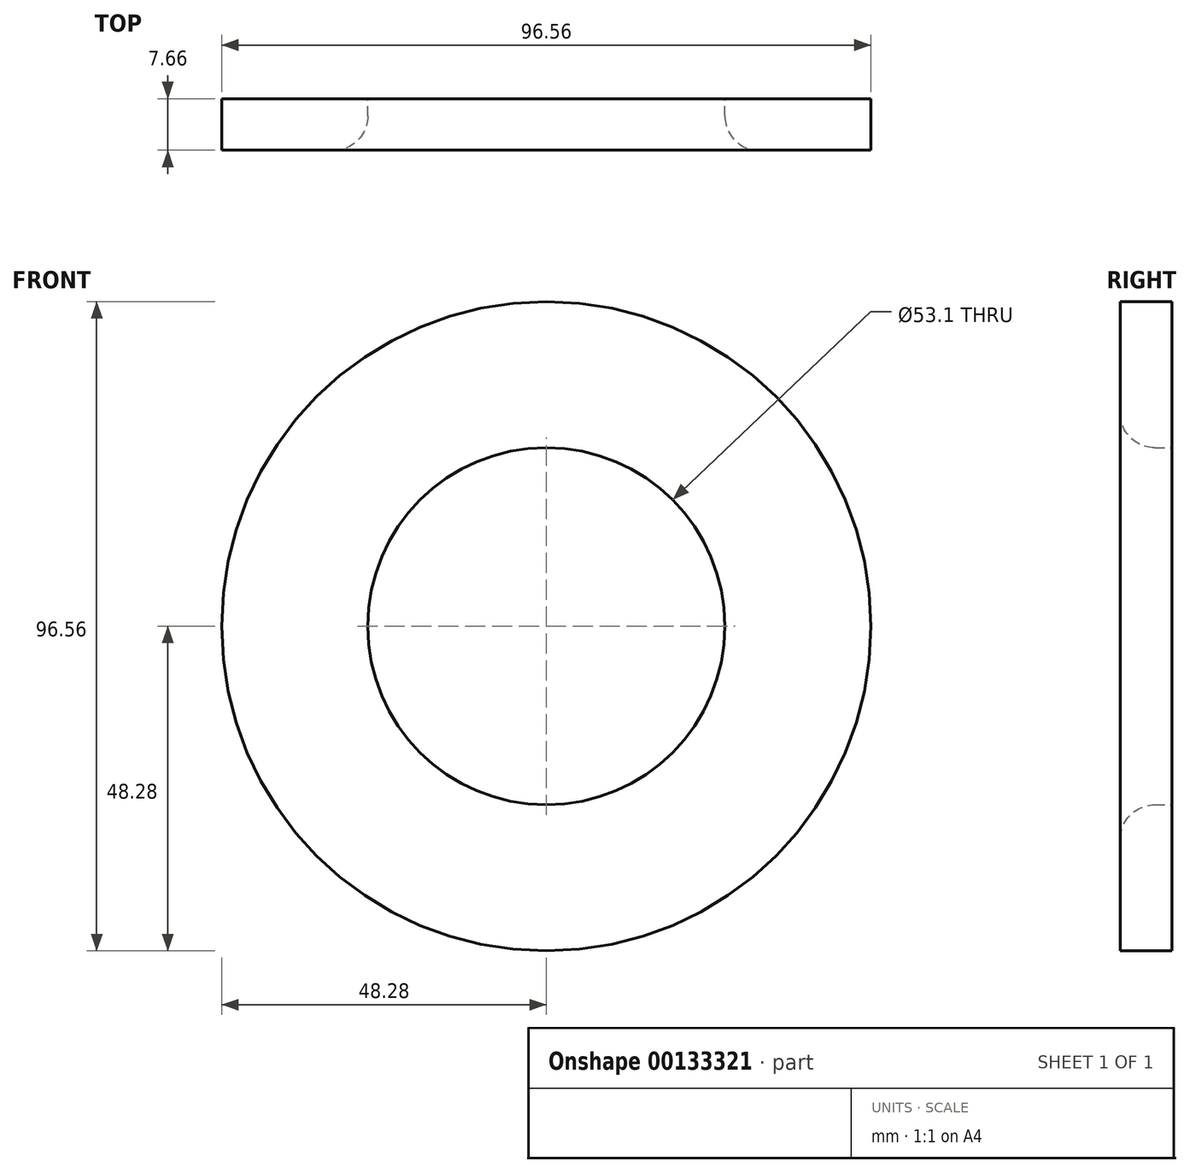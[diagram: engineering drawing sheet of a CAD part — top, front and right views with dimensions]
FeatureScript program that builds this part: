
annotation { "Feature Type Name" : "Feature", "Feature Type Description" : "" }
export const myFeature = defineFeature(function(context is Context, id is Id, definition is map)
    precondition{}
    {
        {
            var Q0;
            Q0=qCreatedBy(makeId("Front.planeOp"),FACE);
            var sketch = newSketch(context, id + "F0", { "sketchPlane" : qUnion([Q0])});
            skCircle(sketch, "E0", {"center": v(0, 0) * mm, "radius": 48.28 * mm});
            skCircle(sketch, "E1.0", {"center": v(0, 0) * mm, "radius": 26.55 * mm});
            skCircle(sketch, "E2.0", {"center": v(0, 0) * mm, "radius": 15.59 * mm});
            skCircle(sketch, "E3.0", {"center": v(0, 0) * mm, "radius": 21.94 * mm});
            skCircle(sketch, "E4.0", {"center": v(0, 0) * mm, "radius": 9.24 * mm});
            skCircle(sketch, "E5.0", {"center": v(0, 0) * mm, "radius": 4.93 * mm});
            skSolve(sketch);
        }
        {
            var Q0;
            Q0 = qSketchRegion(id + "F0", true);
            extrude(context, id + "F1", {"entities" : qUnion([Q0]), "depth" : 7.66 * mm});
        }
        {
            var Q0;
            Q0=makeQuery(id+"F1.opExtrude","CAP_EDGE",EDGE,{"disambiguationData":[OSD([sQuery(id+"F0.wireOp",EDGE,"E1.0")])],"isStart":false});
            fillet(context, id + "F2", {"entities" : qUnion([Q0]), "radius" : 5.08 * mm, "tangentPropagation" : true, "allowEdgeOverflow" : false});
        }
    });
